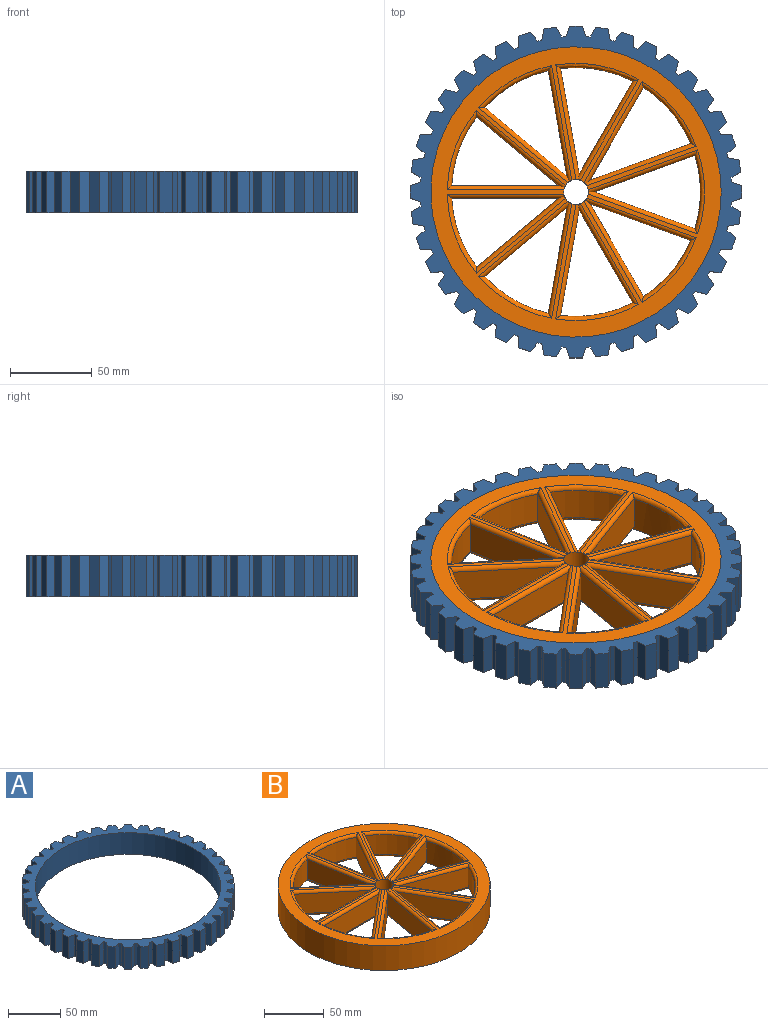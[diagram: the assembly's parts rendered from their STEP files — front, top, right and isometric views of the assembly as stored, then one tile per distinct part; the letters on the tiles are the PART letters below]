
ASSEMBLY  parts=2 mates=1
PART A: 163 faces, bbox 203.2x203.2x25.4 mm
  f0: plane 25.4x5.1mm, normal (0.68,0.73,0), area 177.1mm2, adj f1,f159,f161,f162
  f1: plane 25.4x6.79mm, normal (-0.45,0.89,0), area 193.5mm2, adj f0,f2,f161,f162
  f2: plane 25.4x6.92mm, normal (-0.99,-0.12,0), area 177.1mm2, adj f1,f3,f161,f162
  f3: cylinder r=95.25mm len=25.4mm, axis (0,0,-1), area 65.1mm2, adj f2,f4,f161,f162
  f4: plane 25.4x5.78mm, normal (0.56,0.83,0), area 177.1mm2, adj f3,f5,f161,f162
  f5: plane 25.4x6.16mm, normal (-0.59,0.81,0), area 193.5mm2, adj f4,f6,f161,f162
  f6: plane 25.4x6.7mm, normal (-0.96,-0.28,0), area 177.1mm2, adj f5,f7,f161,f162
  f7: cylinder r=95.25mm len=25.4mm, axis (0,0,-1), area 65.1mm2, adj f6,f8,f161,f162
  f8: plane 25.4x6.32mm, normal (0.42,0.91,0), area 177.1mm2, adj f7,f9,f161,f162
  f9: plane 25.4x5.39mm, normal (-0.71,0.71,0), area 193.5mm2, adj f8,f10,f161,f162
  f10: plane 25.4x6.32mm, normal (-0.91,-0.42,0), area 177.1mm2, adj f9,f11,f161,f162
  f11: cylinder r=95.25mm len=25.4mm, axis (0,0,-1), area 65.1mm2, adj f10,f12,f161,f162
  f12: plane 25.4x6.7mm, normal (0.28,0.96,0), area 177.1mm2, adj f11,f13,f161,f162
  f13: plane 25.4x6.16mm, normal (-0.81,0.59,0), area 193.5mm2, adj f12,f14,f161,f162
  f14: plane 25.4x5.78mm, normal (-0.83,-0.56,0), area 177.1mm2, adj f13,f15,f161,f162
  f15: cylinder r=95.25mm len=25.4mm, axis (0,0,-1), area 65.1mm2, adj f14,f16,f161,f162
  f16: plane 25.4x6.92mm, normal (0.12,0.99,0), area 177.1mm2, adj f15,f17,f161,f162
  f17: plane 25.4x6.79mm, normal (-0.89,0.45,0), area 193.5mm2, adj f16,f18,f161,f162
  f18: plane 25.4x5.1mm, normal (-0.73,-0.68,0), area 177.1mm2, adj f17,f19,f161,f162
  f19: cylinder r=95.25mm len=25.4mm, axis (0,0,-1), area 65.1mm2, adj f18,f20,f161,f162
  f20: plane 25.4x6.97mm, normal (-0.03,1,0), area 177.1mm2, adj f19,f21,f161,f162
  f21: plane 25.4x7.25mm, normal (-0.95,0.31,0), area 193.5mm2, adj f20,f22,f161,f162
  f22: plane 25.4x5.49mm, normal (-0.62,-0.79,0), area 177.1mm2, adj f21,f23,f161,f162
  f23: cylinder r=95.25mm len=25.4mm, axis (0,0,-1), area 65.1mm2, adj f22,f24,f161,f162
  f24: plane 25.4x6.84mm, normal (-0.19,0.98,0), area 177.1mm2, adj f23,f25,f161,f162
  f25: plane 25.4x7.53mm, normal (-0.99,0.16,0), area 193.5mm2, adj f24,f26,f161,f162
  f26: plane 25.4x6.1mm, normal (-0.48,-0.87,0), area 177.1mm2, adj f25,f27,f161,f162
  f27: cylinder r=95.25mm len=25.4mm, axis (0,0,-1), area 65.1mm2, adj f26,f28,f161,f162
  f28: plane 25.4x6.55mm, normal (-0.34,0.94,0), area 177.1mm2, adj f27,f29,f161,f162
  f29: plane 25.4x7.62mm, normal (-1,0,0), area 193.5mm2, adj f28,f30,f161,f162
  f30: plane 25.4x6.55mm, normal (-0.34,-0.94,0), area 177.1mm2, adj f29,f31,f161,f162
  f31: cylinder r=95.25mm len=25.4mm, axis (0,0,-1), area 65.1mm2, adj f30,f32,f161,f162
  f32: plane 25.4x6.1mm, normal (-0.48,0.87,0), area 177.1mm2, adj f31,f33,f161,f162
  f33: plane 25.4x7.53mm, normal (-0.99,-0.16,0), area 193.5mm2, adj f32,f34,f161,f162
  f34: plane 25.4x6.84mm, normal (-0.19,-0.98,0), area 177.1mm2, adj f33,f35,f161,f162
  f35: cylinder r=95.25mm len=25.4mm, axis (0,0,-1), area 65.1mm2, adj f34,f36,f161,f162
  f36: plane 25.4x5.49mm, normal (-0.62,0.79,0), area 177.1mm2, adj f35,f37,f161,f162
  f37: plane 25.4x7.25mm, normal (-0.95,-0.31,0), area 193.5mm2, adj f36,f38,f161,f162
  f38: plane 25.4x6.97mm, normal (-0.03,-1,0), area 177.1mm2, adj f37,f39,f161,f162
  f39: cylinder r=95.25mm len=25.4mm, axis (0,0,-1), area 65.1mm2, adj f38,f40,f161,f162
  f40: plane 25.4x5.1mm, normal (-0.73,0.68,0), area 177.1mm2, adj f39,f41,f161,f162
  f41: plane 25.4x6.79mm, normal (-0.89,-0.45,0), area 193.5mm2, adj f40,f42,f161,f162
  f42: plane 25.4x6.92mm, normal (0.12,-0.99,0), area 177.1mm2, adj f41,f43,f161,f162
  f43: cylinder r=95.25mm len=25.4mm, axis (0,0,-1), area 65.1mm2, adj f42,f44,f161,f162
  f44: plane 25.4x5.78mm, normal (-0.83,0.56,0), area 177.1mm2, adj f43,f45,f161,f162
  f45: plane 25.4x6.16mm, normal (-0.81,-0.59,0), area 193.5mm2, adj f44,f46,f161,f162
  f46: plane 25.4x6.7mm, normal (0.28,-0.96,0), area 177.1mm2, adj f45,f47,f161,f162
  f47: cylinder r=95.25mm len=25.4mm, axis (0,0,-1), area 65.1mm2, adj f46,f48,f161,f162
  f48: plane 25.4x6.32mm, normal (-0.91,0.42,0), area 177.1mm2, adj f47,f49,f161,f162
  f49: plane 25.4x5.39mm, normal (-0.71,-0.71,0), area 193.5mm2, adj f48,f50,f161,f162
  f50: plane 25.4x6.32mm, normal (0.42,-0.91,0), area 177.1mm2, adj f49,f51,f161,f162
  f51: cylinder r=95.25mm len=25.4mm, axis (0,0,-1), area 65.1mm2, adj f50,f52,f161,f162
  f52: plane 25.4x6.7mm, normal (-0.96,0.28,0), area 177.1mm2, adj f51,f53,f161,f162
  f53: plane 25.4x6.16mm, normal (-0.59,-0.81,0), area 193.5mm2, adj f52,f54,f161,f162
  f54: plane 25.4x5.78mm, normal (0.56,-0.83,0), area 177.1mm2, adj f53,f55,f161,f162
  f55: cylinder r=95.25mm len=25.4mm, axis (0,0,-1), area 65.1mm2, adj f54,f56,f161,f162
  f56: plane 25.4x6.92mm, normal (-0.99,0.12,0), area 177.1mm2, adj f55,f57,f161,f162
  f57: plane 25.4x6.79mm, normal (-0.45,-0.89,0), area 193.5mm2, adj f56,f58,f161,f162
  f58: plane 25.4x5.1mm, normal (0.68,-0.73,0), area 177.1mm2, adj f57,f59,f161,f162
  f59: cylinder r=95.25mm len=25.4mm, axis (0,0,-1), area 65.1mm2, adj f58,f60,f161,f162
  f60: plane 25.4x6.97mm, normal (-1,-0.03,0), area 177.1mm2, adj f59,f61,f161,f162
  f61: plane 25.4x7.25mm, normal (-0.31,-0.95,0), area 193.5mm2, adj f60,f62,f161,f162
  f62: plane 25.4x5.49mm, normal (0.79,-0.62,0), area 177.1mm2, adj f61,f63,f161,f162
  f63: cylinder r=95.25mm len=25.4mm, axis (0,0,-1), area 65.1mm2, adj f62,f64,f161,f162
  f64: plane 25.4x6.84mm, normal (-0.98,-0.19,0), area 177.1mm2, adj f63,f65,f161,f162
  f65: plane 25.4x7.53mm, normal (-0.16,-0.99,0), area 193.5mm2, adj f64,f66,f161,f162
  f66: plane 25.4x6.1mm, normal (0.87,-0.48,0), area 177.1mm2, adj f65,f67,f161,f162
  f67: cylinder r=95.25mm len=25.4mm, axis (0,0,-1), area 65.1mm2, adj f66,f68,f161,f162
  f68: plane 25.4x6.55mm, normal (-0.94,-0.34,0), area 177.1mm2, adj f67,f69,f161,f162
  f69: plane 25.4x7.62mm, normal (0,-1,0), area 193.5mm2, adj f68,f70,f161,f162
  f70: plane 25.4x6.55mm, normal (0.94,-0.34,0), area 177.1mm2, adj f69,f71,f161,f162
  f71: cylinder r=95.25mm len=25.4mm, axis (0,0,-1), area 65.1mm2, adj f70,f72,f161,f162
  f72: plane 25.4x6.1mm, normal (-0.87,-0.48,0), area 177.1mm2, adj f71,f73,f161,f162
  f73: plane 25.4x7.53mm, normal (0.16,-0.99,0), area 193.5mm2, adj f72,f74,f161,f162
  f74: plane 25.4x6.84mm, normal (0.98,-0.19,0), area 177.1mm2, adj f73,f75,f161,f162
  f75: cylinder r=95.25mm len=25.4mm, axis (0,0,-1), area 65.1mm2, adj f74,f76,f161,f162
  f76: plane 25.4x5.49mm, normal (-0.79,-0.62,0), area 177.1mm2, adj f75,f77,f161,f162
  f77: plane 25.4x7.25mm, normal (0.31,-0.95,0), area 193.5mm2, adj f76,f78,f161,f162
  f78: plane 25.4x6.97mm, normal (1,-0.03,0), area 177.1mm2, adj f77,f79,f161,f162
  f79: cylinder r=95.25mm len=25.4mm, axis (0,0,-1), area 65.1mm2, adj f78,f80,f161,f162
  f80: plane 25.4x5.1mm, normal (-0.68,-0.73,0), area 177.1mm2, adj f79,f81,f161,f162
  f81: plane 25.4x6.79mm, normal (0.45,-0.89,0), area 193.5mm2, adj f80,f82,f161,f162
  f82: plane 25.4x6.92mm, normal (0.99,0.12,0), area 177.1mm2, adj f81,f83,f161,f162
  f83: cylinder r=95.25mm len=25.4mm, axis (0,0,-1), area 65.1mm2, adj f82,f84,f161,f162
  f84: plane 25.4x5.78mm, normal (-0.56,-0.83,0), area 177.1mm2, adj f83,f85,f161,f162
  f85: plane 25.4x6.16mm, normal (0.59,-0.81,0), area 193.5mm2, adj f84,f86,f161,f162
  f86: plane 25.4x6.7mm, normal (0.96,0.28,0), area 177.1mm2, adj f85,f87,f161,f162
  f87: cylinder r=95.25mm len=25.4mm, axis (0,0,-1), area 65.1mm2, adj f86,f88,f161,f162
  f88: plane 25.4x6.32mm, normal (-0.42,-0.91,0), area 177.1mm2, adj f87,f89,f161,f162
  f89: plane 25.4x5.39mm, normal (0.71,-0.71,0), area 193.5mm2, adj f88,f90,f161,f162
  f90: plane 25.4x6.32mm, normal (0.91,0.42,0), area 177.1mm2, adj f89,f91,f161,f162
  f91: cylinder r=95.25mm len=25.4mm, axis (0,0,-1), area 65.1mm2, adj f90,f92,f161,f162
  f92: plane 25.4x6.7mm, normal (-0.28,-0.96,0), area 177.1mm2, adj f91,f93,f161,f162
  f93: plane 25.4x6.16mm, normal (0.81,-0.59,0), area 193.5mm2, adj f92,f94,f161,f162
  f94: plane 25.4x5.78mm, normal (0.83,0.56,0), area 177.1mm2, adj f93,f95,f161,f162
  f95: cylinder r=95.25mm len=25.4mm, axis (0,0,-1), area 65.1mm2, adj f94,f96,f161,f162
  f96: plane 25.4x6.92mm, normal (-0.12,-0.99,0), area 177.1mm2, adj f95,f97,f161,f162
  f97: plane 25.4x6.79mm, normal (0.89,-0.45,0), area 193.5mm2, adj f96,f98,f161,f162
  f98: plane 25.4x5.1mm, normal (0.73,0.68,0), area 177.1mm2, adj f97,f99,f161,f162
  f99: cylinder r=95.25mm len=25.4mm, axis (0,0,-1), area 65.1mm2, adj f98,f100,f161,f162
  f100: plane 25.4x6.97mm, normal (0.03,-1,0), area 177.1mm2, adj f99,f101,f161,f162
  f101: plane 25.4x7.25mm, normal (0.95,-0.31,0), area 193.5mm2, adj f100,f102,f161,f162
  f102: plane 25.4x5.49mm, normal (0.62,0.79,0), area 177.1mm2, adj f101,f103,f161,f162
  f103: cylinder r=95.25mm len=25.4mm, axis (0,0,-1), area 65.1mm2, adj f102,f104,f161,f162
  f104: plane 25.4x6.84mm, normal (0.19,-0.98,0), area 177.1mm2, adj f103,f105,f161,f162
  f105: plane 25.4x7.53mm, normal (0.99,-0.16,0), area 193.5mm2, adj f104,f106,f161,f162
  f106: plane 25.4x6.1mm, normal (0.48,0.87,0), area 177.1mm2, adj f105,f107,f161,f162
  f107: cylinder r=95.25mm len=25.4mm, axis (0,0,-1), area 65.1mm2, adj f106,f108,f161,f162
  f108: plane 25.4x6.55mm, normal (0.34,-0.94,0), area 177.1mm2, adj f107,f109,f161,f162
  f109: plane 25.4x7.62mm, normal (1,0,0), area 193.5mm2, adj f108,f110,f161,f162
  f110: plane 25.4x6.55mm, normal (0.34,0.94,0), area 177.1mm2, adj f109,f111,f161,f162
  f111: cylinder r=95.25mm len=25.4mm, axis (0,0,-1), area 65.1mm2, adj f110,f112,f161,f162
  f112: plane 25.4x6.1mm, normal (0.48,-0.87,0), area 177.1mm2, adj f111,f113,f161,f162
  f113: plane 25.4x7.53mm, normal (0.99,0.16,0), area 193.5mm2, adj f112,f114,f161,f162
  f114: plane 25.4x6.84mm, normal (0.19,0.98,0), area 177.1mm2, adj f113,f115,f161,f162
  f115: cylinder r=95.25mm len=25.4mm, axis (0,0,-1), area 65.1mm2, adj f114,f116,f161,f162
  f116: plane 25.4x5.49mm, normal (0.62,-0.79,0), area 177.1mm2, adj f115,f117,f161,f162
  f117: plane 25.4x7.25mm, normal (0.95,0.31,0), area 193.5mm2, adj f116,f118,f161,f162
  f118: plane 25.4x6.97mm, normal (0.03,1,0), area 177.1mm2, adj f117,f119,f161,f162
  f119: cylinder r=95.25mm len=25.4mm, axis (0,0,-1), area 65.1mm2, adj f118,f120,f161,f162
  f120: plane 25.4x5.1mm, normal (0.73,-0.68,0), area 177.1mm2, adj f119,f121,f161,f162
  f121: plane 25.4x6.79mm, normal (0.89,0.45,0), area 193.5mm2, adj f120,f122,f161,f162
  f122: plane 25.4x6.92mm, normal (-0.12,0.99,0), area 177.1mm2, adj f121,f123,f161,f162
  f123: cylinder r=95.25mm len=25.4mm, axis (0,0,-1), area 65.1mm2, adj f122,f124,f161,f162
  f124: plane 25.4x5.78mm, normal (0.83,-0.56,0), area 177.1mm2, adj f123,f125,f161,f162
  f125: plane 25.4x6.16mm, normal (0.81,0.59,0), area 193.5mm2, adj f124,f126,f161,f162
  f126: plane 25.4x6.7mm, normal (-0.28,0.96,0), area 177.1mm2, adj f125,f127,f161,f162
  f127: cylinder r=95.25mm len=25.4mm, axis (0,0,-1), area 65.1mm2, adj f126,f128,f161,f162
  f128: plane 25.4x6.32mm, normal (0.91,-0.42,0), area 177.1mm2, adj f127,f129,f161,f162
  f129: plane 25.4x5.39mm, normal (0.71,0.71,0), area 193.5mm2, adj f128,f130,f161,f162
  f130: plane 25.4x6.32mm, normal (-0.42,0.91,0), area 177.1mm2, adj f129,f131,f161,f162
  f131: cylinder r=95.25mm len=25.4mm, axis (0,0,-1), area 65.1mm2, adj f130,f132,f161,f162
  f132: plane 25.4x6.7mm, normal (0.96,-0.28,0), area 177.1mm2, adj f131,f133,f161,f162
  f133: plane 25.4x6.16mm, normal (0.59,0.81,0), area 193.5mm2, adj f132,f134,f161,f162
  f134: plane 25.4x5.78mm, normal (-0.56,0.83,0), area 177.1mm2, adj f133,f135,f161,f162
  f135: cylinder r=95.25mm len=25.4mm, axis (0,0,-1), area 65.1mm2, adj f134,f136,f161,f162
  f136: plane 25.4x6.92mm, normal (0.99,-0.12,0), area 177.1mm2, adj f135,f137,f161,f162
  f137: plane 25.4x6.79mm, normal (0.45,0.89,0), area 193.5mm2, adj f136,f138,f161,f162
  f138: plane 25.4x5.1mm, normal (-0.68,0.73,0), area 177.1mm2, adj f137,f139,f161,f162
  f139: cylinder r=95.25mm len=25.4mm, axis (0,0,-1), area 65.1mm2, adj f138,f140,f161,f162
  f140: plane 25.4x6.97mm, normal (1,0.03,0), area 177.1mm2, adj f139,f141,f161,f162
  f141: plane 25.4x7.25mm, normal (0.31,0.95,0), area 193.5mm2, adj f140,f142,f161,f162
  f142: plane 25.4x5.49mm, normal (-0.79,0.62,0), area 177.1mm2, adj f141,f143,f161,f162
  f143: cylinder r=95.25mm len=25.4mm, axis (0,0,-1), area 65.1mm2, adj f142,f144,f161,f162
  f144: plane 25.4x6.84mm, normal (0.98,0.19,0), area 177.1mm2, adj f143,f145,f161,f162
  f145: plane 25.4x7.53mm, normal (0.16,0.99,0), area 193.5mm2, adj f144,f146,f161,f162
  f146: plane 25.4x6.1mm, normal (-0.87,0.48,0), area 177.1mm2, adj f145,f147,f161,f162
  f147: cylinder r=95.25mm len=25.4mm, axis (0,0,-1), area 65.1mm2, adj f146,f148,f161,f162
  f148: plane 25.4x6.55mm, normal (0.94,0.34,0), area 177.1mm2, adj f147,f149,f161,f162
  f149: plane 25.4x7.62mm, normal (0,1,0), area 193.5mm2, adj f148,f150,f161,f162
  f150: plane 25.4x6.55mm, normal (-0.94,0.34,0), area 177.1mm2, adj f149,f151,f161,f162
  f151: cylinder r=95.25mm len=25.4mm, axis (0,0,-1), area 65.1mm2, adj f150,f152,f161,f162
  f152: plane 25.4x6.1mm, normal (0.87,0.48,0), area 177.1mm2, adj f151,f153,f161,f162
  f153: plane 25.4x7.53mm, normal (-0.16,0.99,0), area 193.5mm2, adj f152,f154,f161,f162
  f154: plane 25.4x6.84mm, normal (-0.98,0.19,0), area 177.1mm2, adj f153,f155,f161,f162
  f155: cylinder r=95.25mm len=25.4mm, axis (0,0,-1), area 65.1mm2, adj f154,f156,f161,f162
  f156: plane 25.4x5.49mm, normal (0.79,0.62,0), area 177.1mm2, adj f155,f157,f161,f162
  f157: plane 25.4x7.25mm, normal (-0.31,0.95,0), area 193.5mm2, adj f156,f158,f161,f162
  f158: plane 25.4x6.97mm, normal (-1,0.03,0), area 177.1mm2, adj f157,f159,f161,f162
  f159: cylinder r=95.25mm len=25.4mm, axis (0,0,-1), area 65.1mm2, adj f0,f158,f161,f162
  f160: cylinder r=88.9mm len=177.8mm, axis (0,0,-1), area 14187.8mm2, adj f161,f162
  f161: plane 203.2x203.2mm, normal (0,0,1), area 6228.9mm2, adj f0,f1,f2,f3,f4,f5,f6,f7
  f162: plane 203.2x203.2mm, normal (0,0,-1), area 6228.9mm2, adj f0,f1,f2,f3,f4,f5,f6,f7
PART B: 84 faces, bbox 177.8x177.8x25.4 mm
  f0: plane 56.84x32.82mm, normal (0.87,-0.5,0), area 1333.7mm2, adj f1,f19,f50,f77
  f1: cylinder r=76.2mm len=34.39mm, axis (0,0,-1), area 926.1mm2, adj f0,f19,f51,f78
  f2: cylinder r=76.2mm len=44.22mm, axis (0,0,-1), area 926.1mm2, adj f3,f20,f48,f75
  f3: plane 56.84x32.82mm, normal (-0.87,0.5,0), area 1333.7mm2, adj f2,f20,f46,f73
  f4: cylinder r=76.2mm len=38.88mm, axis (0,0,-1), area 926.1mm2, adj f5,f21,f45,f72
  f5: plane 64.64x20.32mm, normal (-0.98,-0.17,0), area 1333.7mm2, adj f4,f21,f43,f70
  f6: cylinder r=76.2mm len=42.19mm, axis (0,0,-1), area 926.1mm2, adj f7,f22,f42,f69
  f7: plane 50.28x42.19mm, normal (-0.64,-0.77,0), area 1333.7mm2, adj f6,f22,f40,f67
  f8: cylinder r=76.2mm len=42.19mm, axis (0,0,-1), area 926.1mm2, adj f9,f23,f39,f66
  f9: plane 65.64x20.32mm, normal (0,-1,0), area 1333.7mm2, adj f8,f23,f37,f64
  f10: cylinder r=76.2mm len=38.88mm, axis (0,0,-1), area 926.1mm2, adj f11,f24,f36,f63
  f11: plane 50.28x42.19mm, normal (0.64,-0.77,0), area 1333.7mm2, adj f10,f24,f34,f61
  f12: cylinder r=76.2mm len=44.22mm, axis (0,0,-1), area 926.1mm2, adj f13,f25,f33,f60
  f13: plane 64.64x20.32mm, normal (0.98,-0.17,0), area 1333.7mm2, adj f12,f25,f31,f58
  f14: cylinder r=76.2mm len=34.39mm, axis (0,0,-1), area 926.1mm2, adj f15,f26,f56,f82
  f15: plane 56.84x32.82mm, normal (0.87,0.5,0), area 1333.7mm2, adj f14,f26,f57,f83
  f16: cylinder r=76.2mm len=49.73mm, axis (0,0,-1), area 1044.6mm2, adj f17,f27,f30,f54,f79,f80
  f17: plane 61.68x22.45mm, normal (0.34,0.94,0), area 1333.7mm2, adj f16,f27,f52,f79
  f18: cylinder r=88.9mm len=177.8mm, axis (0,0,-1), area 14187.8mm2, adj f29,f30
  f19: plane 61.68x22.45mm, normal (-0.34,0.94,0), area 1333.7mm2, adj f0,f1,f49,f76
  f20: plane 64.64x20.32mm, normal (0.98,0.17,0), area 1333.7mm2, adj f2,f3,f47,f74
  f21: plane 50.28x42.19mm, normal (0.64,0.77,0), area 1333.7mm2, adj f4,f5,f44,f71
  f22: plane 65.64x20.32mm, normal (0,1,0), area 1333.7mm2, adj f6,f7,f41,f68
  f23: plane 50.28x42.19mm, normal (-0.64,0.77,0), area 1333.7mm2, adj f8,f9,f38,f65
  f24: plane 64.64x20.32mm, normal (-0.98,0.17,0), area 1333.7mm2, adj f10,f11,f35,f62
  f25: plane 56.84x32.82mm, normal (-0.87,-0.5,0), area 1333.7mm2, adj f12,f13,f32,f59
  f26: plane 61.68x22.45mm, normal (-0.34,-0.94,0), area 1333.7mm2, adj f14,f15,f55,f81
  f27: plane 61.68x22.45mm, normal (0.34,-0.94,0), area 1333.7mm2, adj f16,f17,f53,f80
  f28: cylinder r=7.62mm len=25.4mm, axis (0,0,-1), area 1209.9mm2, adj f29,f30,f31,f32,f34,f35,f37,f38
  f29: plane 177.8x177.8mm, normal (0,0,1), area 6977.4mm2, adj f18,f28,f31,f32,f33,f34,f35,f36
  f30: plane 177.8x177.8mm, normal (0,0,-1), area 7108.3mm2, adj f16,f18,f28,f58,f59,f60,f61,f62
  f31: cylinder r=2.54mm len=70.92mm, axis (-0.17,-0.98,0), area 273.1mm2, adj f13,f28,f29,f32,f33
  f32: cylinder r=2.54mm len=63.25mm, axis (-0.5,0.87,0), area 273.1mm2, adj f25,f28,f29,f31,f33
  f33: torus R=78.74mm, axis (0,0,1), area 191.8mm2, adj f12,f29,f31,f32
  f34: cylinder r=2.54mm len=56.46mm, axis (-0.77,-0.64,0), area 273.1mm2, adj f11,f28,f29,f35,f36
  f35: cylinder r=2.54mm len=70.92mm, axis (0.17,0.98,0), area 273.1mm2, adj f24,f28,f29,f34,f36
  f36: torus R=78.74mm, axis (0,0,1), area 191.8mm2, adj f10,f29,f34,f35
  f37: cylinder r=2.54mm len=71.57mm, axis (-1,0,0), area 273.1mm2, adj f9,f28,f29,f38,f39
  f38: cylinder r=2.54mm len=56.46mm, axis (0.77,0.64,0), area 273.1mm2, adj f23,f28,f29,f37,f39
  f39: torus R=78.74mm, axis (0,0,1), area 191.8mm2, adj f8,f29,f37,f38
  f40: cylinder r=2.54mm len=56.46mm, axis (-0.77,0.64,0), area 273.1mm2, adj f7,f28,f29,f41,f42
  f41: cylinder r=2.54mm len=71.57mm, axis (1,0,0), area 273.1mm2, adj f22,f28,f29,f40,f42
  f42: torus R=78.74mm, axis (0,0,1), area 191.8mm2, adj f6,f29,f40,f41
  f43: cylinder r=2.54mm len=70.92mm, axis (-0.17,0.98,0), area 273.1mm2, adj f5,f28,f29,f44,f45
  f44: cylinder r=2.54mm len=56.46mm, axis (0.77,-0.64,0), area 273.1mm2, adj f21,f28,f29,f43,f45
  f45: torus R=78.74mm, axis (0,0,1), area 191.8mm2, adj f4,f29,f43,f44
  f46: cylinder r=2.54mm len=63.25mm, axis (0.5,0.87,0), area 273.1mm2, adj f3,f28,f29,f47,f48
  f47: cylinder r=2.54mm len=70.92mm, axis (0.17,-0.98,0), area 273.1mm2, adj f20,f28,f29,f46,f48
  f48: torus R=78.74mm, axis (0,0,1), area 191.8mm2, adj f2,f29,f46,f47
  f49: cylinder r=2.54mm len=68.12mm, axis (0.94,0.34,0), area 273.1mm2, adj f19,f28,f29,f50,f51
  f50: cylinder r=2.54mm len=63.25mm, axis (-0.5,-0.87,0), area 273.1mm2, adj f0,f28,f29,f49,f51
  f51: torus R=78.74mm, axis (0,0,1), area 191.8mm2, adj f1,f29,f49,f50
  f52: cylinder r=2.54mm len=68.12mm, axis (0.94,-0.34,0), area 273.1mm2, adj f17,f28,f29,f53,f54
  f53: cylinder r=2.54mm len=68.12mm, axis (-0.94,-0.34,0), area 273.1mm2, adj f27,f28,f29,f52,f54
  f54: torus R=78.74mm, axis (0,0,1), area 191.8mm2, adj f16,f29,f52,f53
  f55: cylinder r=2.54mm len=68.12mm, axis (-0.94,0.34,0), area 273.1mm2, adj f26,f28,f29,f56,f57
  f56: torus R=78.74mm, axis (0,0,1), area 191.8mm2, adj f14,f29,f55,f57
  f57: cylinder r=2.54mm len=63.25mm, axis (0.5,-0.87,0), area 273.1mm2, adj f15,f28,f29,f55,f56
  f58: cylinder r=2.54mm len=70.92mm, axis (0.17,0.98,0), area 273.1mm2, adj f13,f28,f30,f59,f60
  f59: cylinder r=2.54mm len=63.25mm, axis (0.5,-0.87,0), area 273.1mm2, adj f25,f28,f30,f58,f60
  f60: torus R=78.74mm, axis (0,0,1), area 191.8mm2, adj f12,f30,f58,f59
  f61: cylinder r=2.54mm len=56.46mm, axis (0.77,0.64,0), area 273.1mm2, adj f11,f28,f30,f62,f63
  f62: cylinder r=2.54mm len=70.92mm, axis (-0.17,-0.98,0), area 273.1mm2, adj f24,f28,f30,f61,f63
  f63: torus R=78.74mm, axis (0,0,1), area 191.8mm2, adj f10,f30,f61,f62
  f64: cylinder r=2.54mm len=71.57mm, axis (1,0,0), area 273.1mm2, adj f9,f28,f30,f65,f66
  f65: cylinder r=2.54mm len=56.46mm, axis (-0.77,-0.64,0), area 273.1mm2, adj f23,f28,f30,f64,f66
  f66: torus R=78.74mm, axis (0,0,1), area 191.8mm2, adj f8,f30,f64,f65
  f67: cylinder r=2.54mm len=56.46mm, axis (0.77,-0.64,0), area 273.1mm2, adj f7,f28,f30,f68,f69
  f68: cylinder r=2.54mm len=71.57mm, axis (-1,0,0), area 273.1mm2, adj f22,f28,f30,f67,f69
  f69: torus R=78.74mm, axis (0,0,1), area 191.8mm2, adj f6,f30,f67,f68
  f70: cylinder r=2.54mm len=70.92mm, axis (0.17,-0.98,0), area 273.1mm2, adj f5,f28,f30,f71,f72
  f71: cylinder r=2.54mm len=56.46mm, axis (-0.77,0.64,0), area 273.1mm2, adj f21,f28,f30,f70,f72
  f72: torus R=78.74mm, axis (0,0,1), area 191.8mm2, adj f4,f30,f70,f71
  f73: cylinder r=2.54mm len=63.25mm, axis (-0.5,-0.87,0), area 273.1mm2, adj f3,f28,f30,f74,f75
  f74: cylinder r=2.54mm len=70.92mm, axis (-0.17,0.98,0), area 273.1mm2, adj f20,f28,f30,f73,f75
  f75: torus R=78.74mm, axis (0,0,1), area 191.8mm2, adj f2,f30,f73,f74
  f76: cylinder r=2.54mm len=68.12mm, axis (-0.94,-0.34,0), area 273.1mm2, adj f19,f28,f30,f77,f78
  f77: cylinder r=2.54mm len=63.25mm, axis (0.5,0.87,0), area 273.1mm2, adj f0,f28,f30,f76,f78
  f78: torus R=78.74mm, axis (0,0,1), area 191.8mm2, adj f1,f30,f76,f77
  f79: cylinder r=2.54mm len=65.73mm, axis (-0.94,0.34,0), area 269.4mm2, adj f16,f17,f28,f30,f80
  f80: cylinder r=2.54mm len=65.73mm, axis (0.94,0.34,0), area 269.4mm2, adj f16,f27,f28,f30,f79
  f81: cylinder r=2.54mm len=68.12mm, axis (0.94,-0.34,0), area 273.1mm2, adj f26,f28,f30,f82,f83
  f82: torus R=78.74mm, axis (0,0,1), area 191.8mm2, adj f14,f30,f81,f83
  f83: cylinder r=2.54mm len=63.25mm, axis (-0.5,0.87,0), area 273.1mm2, adj f15,f28,f30,f81,f82
PLACE A at identity
PLACE B at identity
MATE fastened A.f160 <-> B.f28  axis (0,0,-1) through (0,0,25.4)mm
